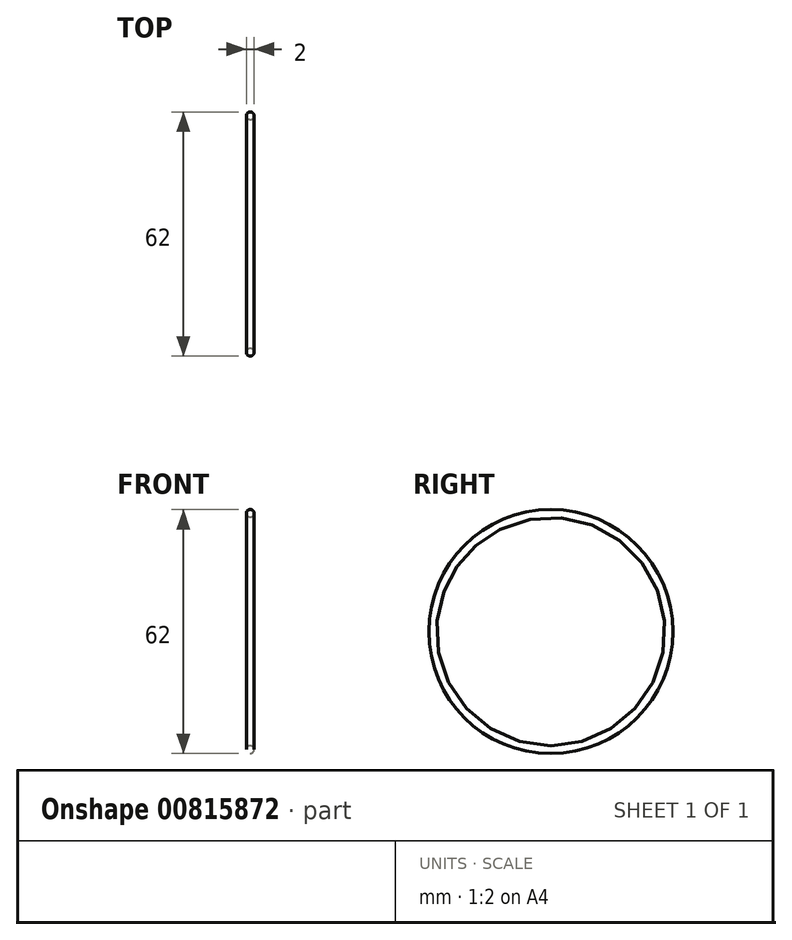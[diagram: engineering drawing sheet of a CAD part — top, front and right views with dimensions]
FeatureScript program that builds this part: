
annotation { "Feature Type Name" : "Feature", "Feature Type Description" : "" }
export const myFeature = defineFeature(function(context is Context, id is Id, definition is map)
    precondition{}
    {
        {
            var Q0;
            Q0=qCreatedBy(makeId("Front.planeOp"),FACE);
            var sketch = newSketch(context, id + "F0", { "sketchPlane" : qUnion([Q0])});
            skCircle(sketch, "E0", {"center": v(0, 30) * mm, "radius": 1 * mm});
            skLineSegment(sketch, "E1", {"start": v(-13.43, 0) * mm, "end": v(13.43, 0) * mm, "construction": true});
            skSolve(sketch);
        }
        {
            var Q0;
            Q0=sQuery(id+"F0.wireOp",EDGE,"E0");
            var Q1;
            Q1=sQuery(id+"F0.wireOp",EDGE,"E1");
            revolve(context, id + "F1", {"bodyType" : ToolBodyType.SURFACE, "surfaceOperationType" : NewSurfaceOperationType.NEW, "surfaceEntities" : qUnion([Q0]), "axis" : qUnion([Q1]), "revolveType" : RevolveType.FULL});
        }
    });
